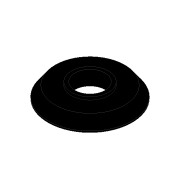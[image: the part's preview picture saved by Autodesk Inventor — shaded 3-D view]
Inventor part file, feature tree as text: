
AUTODESK INVENTOR PART (.ipt)
format: ipt  version: 2020 (Build 240168000, 168)  size: 104,960 bytes
history: native  units: in
note: dims shown in document units (in); Inventor stores cm internally (conversion verified against a paired STEP export)
features: extrude x2, sketch x2, chamfer x1
ambient origin geometry x8: Origin, YZ Plane, XZ Plane, XY Plane, X Axis, Y Axis, Z Axis, Center Point
bodies: Solid1 (feature_tree)
feature tree (5):
  extrude  "Extrusion1"  Depth=0.0787in
  chamfer  "Chamfer1"  Distance=0.0787in
  extrude  "Extrusion2"  Depth=0.0197in
  sketch  "Sketch1"  dims[d0=0.2047in d1=0.5709in d2=0.0787in d3=0.0in]
  sketch  "Sketch2"  dims[d4=0.0492in d5=0.0689in d6=45.0deg d7=0.0236in d8=0.0197in d9=0.0in]
